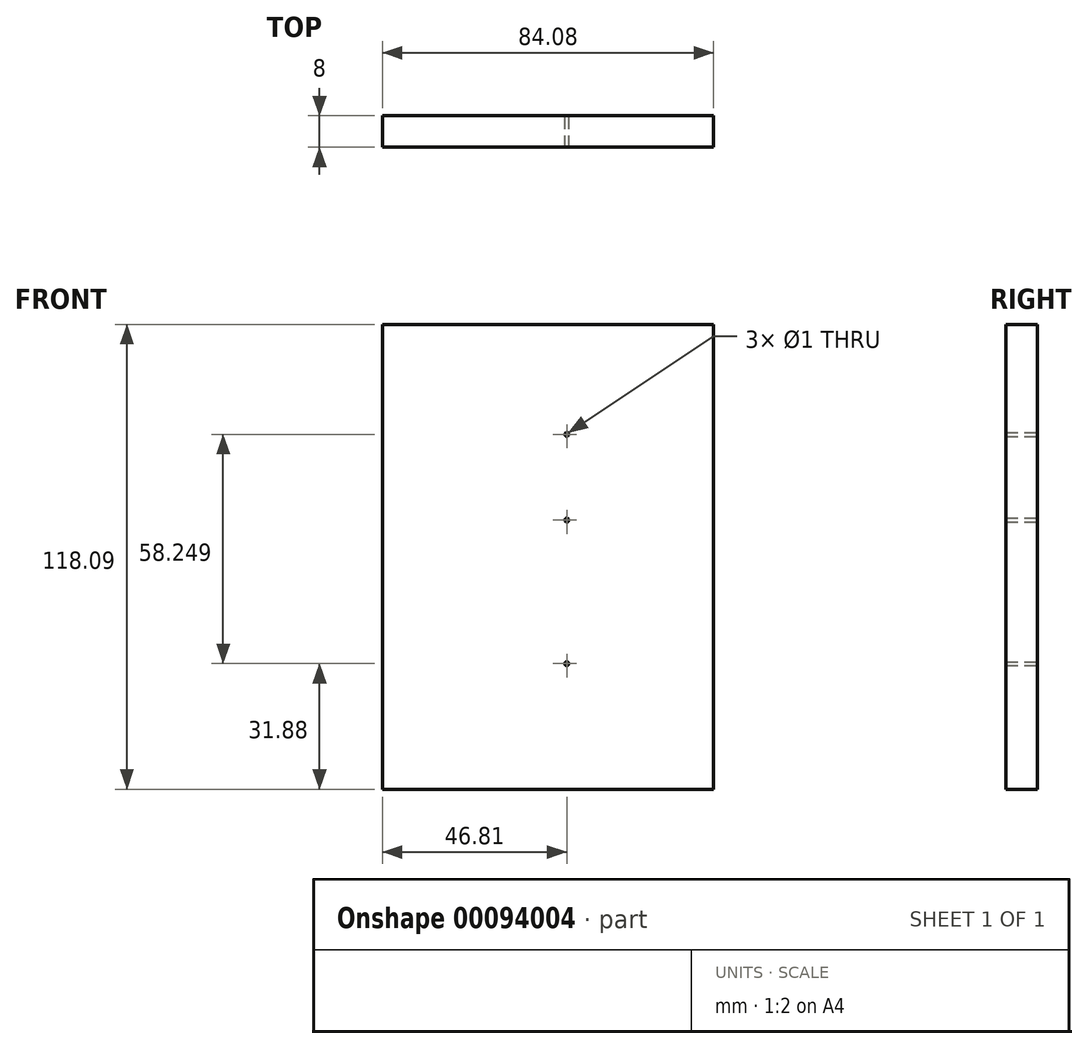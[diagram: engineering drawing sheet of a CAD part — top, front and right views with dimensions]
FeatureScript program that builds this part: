
annotation { "Feature Type Name" : "Feature", "Feature Type Description" : "" }
export const myFeature = defineFeature(function(context is Context, id is Id, definition is map)
    precondition{}
    {
        {
            var Q0;
            Q0=qCreatedBy(makeId("Front.planeOp"),FACE);
            var sketch = newSketch(context, id + "F0", { "sketchPlane" : qUnion([Q0])});
            skCircle(sketch, "E0", {"center": v(0, 21.75) * mm, "radius": 0.5 * mm});
            skLineSegment(sketch, "E1.bottom", {"start": v(-46.8, 49.7) * mm, "end": v(37.27, 49.7) * mm});
            skLineSegment(sketch, "E1.top", {"start": v(-46.8, -68.38) * mm, "end": v(37.27, -68.38) * mm});
            skLineSegment(sketch, "E1.left", {"start": v(-46.8, 49.7) * mm, "end": v(-46.8, -68.38) * mm});
            skLineSegment(sketch, "E1.right", {"start": v(37.27, 49.7) * mm, "end": v(37.27, -68.38) * mm});
            skCircle(sketch, "E2", {"center": v(0, -36.5) * mm, "radius": 0.5 * mm});
            skCircle(sketch, "E3", {"center": v(0, 0) * mm, "radius": 0.5 * mm});
            skSolve(sketch);
        }
        {
            var Q0;
            Q0=makeQuery(id+"F0.imprint","IMPRINT",FACE,{"disambiguationData":[TD([[makeQuery(id+"F0.imprint","IMPRINT",EDGE,{"derivedFrom":sQuery(id+"F0.wireOp",EDGE,"E0")}),-1.0]])]});
            extrude(context, id + "F1", {"entities" : qUnion([Q0]), "depth" : 8 * mm});
        }
    });
